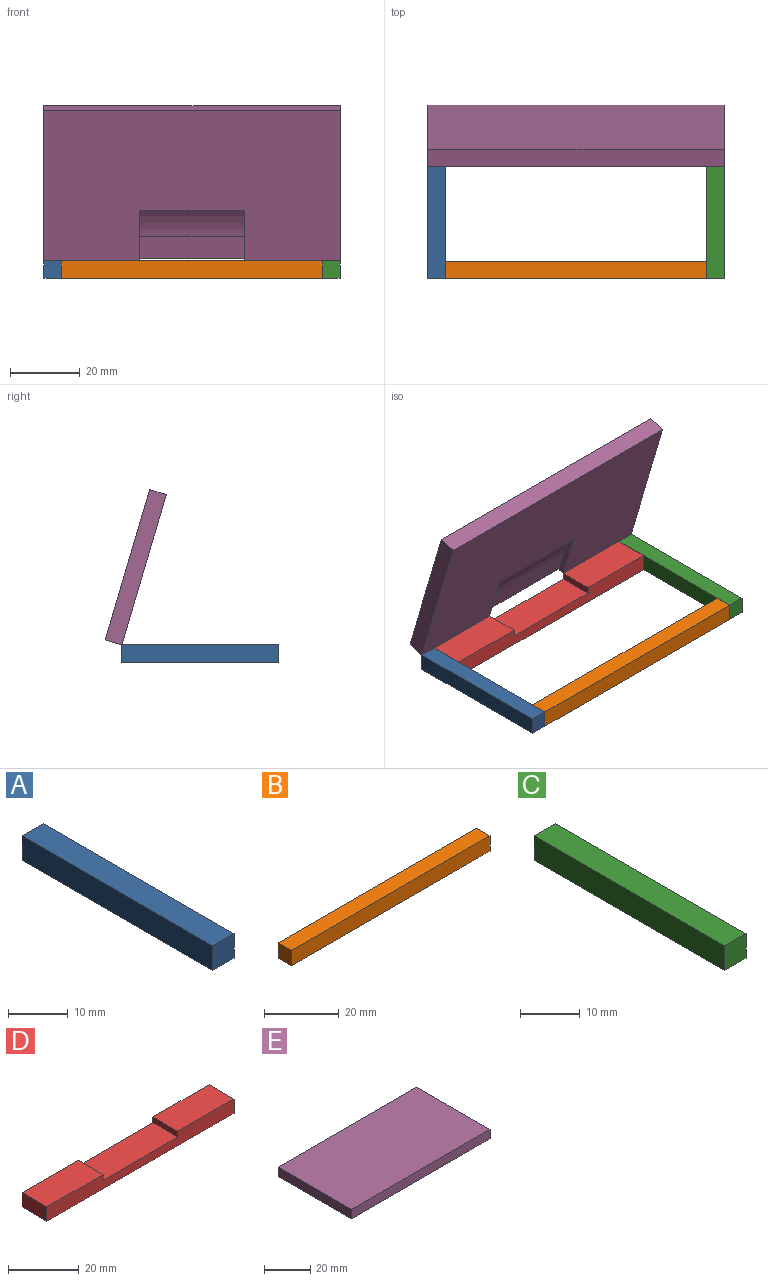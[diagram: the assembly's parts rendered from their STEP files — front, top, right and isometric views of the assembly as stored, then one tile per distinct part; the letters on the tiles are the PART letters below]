
ASSEMBLY  parts=5 mates=4
PART A: 6 faces, bbox 5x45x5 mm
  f0: plane 45x5mm, normal (1,0,0), area 225mm2, adj f1,f3,f4,f5
  f1: plane 5x5mm, normal (0,1,0), area 25mm2, adj f0,f2,f4,f5
  f2: plane 45x5mm, normal (-1,0,0), area 225mm2, adj f1,f3,f4,f5
  f3: plane 5x5mm, normal (0,-1,0), area 25mm2, adj f0,f2,f4,f5
  f4: plane 45x5mm, normal (0,0,1), area 225mm2, adj f0,f1,f2,f3
  f5: plane 45x5mm, normal (0,0,-1), area 225mm2, adj f0,f1,f2,f3
PART B: 6 faces, bbox 75x5x5 mm
  f0: plane 75x5mm, normal (0,1,0), area 375mm2, adj f1,f3,f4,f5
  f1: plane 5x5mm, normal (-1,0,0), area 25mm2, adj f0,f2,f4,f5
  f2: plane 75x5mm, normal (0,-1,0), area 375mm2, adj f1,f3,f4,f5
  f3: plane 5x5mm, normal (1,0,0), area 25mm2, adj f0,f2,f4,f5
  f4: plane 75x5mm, normal (0,0,1), area 375mm2, adj f0,f1,f2,f3
  f5: plane 75x5mm, normal (0,0,-1), area 375mm2, adj f0,f1,f2,f3
PART C: 6 faces, bbox 5x45x5 mm
  f0: plane 45x5mm, normal (-1,0,0), area 225mm2, adj f1,f3,f4,f5
  f1: plane 5x5mm, normal (0,-1,0), area 25mm2, adj f0,f2,f4,f5
  f2: plane 45x5mm, normal (1,0,0), area 225mm2, adj f1,f3,f4,f5
  f3: plane 5x5mm, normal (0,1,0), area 25mm2, adj f0,f2,f4,f5
  f4: plane 45x5mm, normal (0,0,1), area 225mm2, adj f0,f1,f2,f3
  f5: plane 45x5mm, normal (0,0,-1), area 225mm2, adj f0,f1,f2,f3
PART D: 10 faces, bbox 75x10x5 mm
  f0: plane 22.5x10mm, normal (0,0,1), area 225mm2, adj f1,f3,f4,f8
  f1: plane 75x5mm, normal (0,1,0), area 315mm2, adj f0,f2,f4,f5,f6,f7,f8,f9
  f2: plane 10x5mm, normal (-1,0,0), area 50mm2, adj f1,f3,f5,f6
  f3: plane 75x5mm, normal (0,-1,0), area 315mm2, adj f0,f2,f4,f5,f6,f7,f8,f9
  f4: plane 10x5mm, normal (1,0,0), area 50mm2, adj f0,f1,f3,f6
  f5: plane 22.5x10mm, normal (0,0,1), area 225mm2, adj f1,f2,f3,f7
  f6: plane 75x10mm, normal (0,0,-1), area 750mm2, adj f1,f2,f3,f4
  f7: plane 10x2mm, normal (1,0,0), area 20mm2, adj f1,f3,f5,f9
  f8: plane 10x2mm, normal (-1,0,0), area 20mm2, adj f0,f1,f3,f9
  f9: plane 30x10mm, normal (0,0,1), area 300mm2, adj f1,f3,f7,f8
PART E: 10 faces, bbox 85x45x5 mm
  f0: plane 85x5mm, normal (0,1,0), area 365mm2, adj f1,f2,f4,f5,f6,f7,f8
  f1: plane 85x45mm, normal (0,0,-1), area 3375mm2, adj f0,f2,f3,f4,f6,f7,f9
  f2: plane 45x5mm, normal (-1,0,0), area 225mm2, adj f0,f1,f3,f5
  f3: plane 85x5mm, normal (0,-1,0), area 425mm2, adj f1,f2,f4,f5
  f4: plane 45x5mm, normal (1,0,0), area 225mm2, adj f0,f1,f3,f5
  f5: plane 85x45mm, normal (0,0,1), area 3825mm2, adj f0,f2,f3,f4
  f6: plane 15x2mm, normal (1,0,0), area 24.6mm2, adj f0,f1,f8,f9
  f7: plane 15x2mm, normal (-1,0,0), area 24.6mm2, adj f0,f1,f8,f9
  f8: plane 30x6.75mm, normal (0,0,-1), area 202.6mm2, adj f0,f6,f7,f9
  f9: cylinder r=18mm len=30mm, axis (1,0,0), area 257mm2, adj f1,f6,f7,f8
PLACE A t=(0,-20,0)mm
PLACE B rot(axis=(0,1,0),180deg) t=(0,-20,5)mm
PLACE C t=(0,-20,0)mm
PLACE D t=(0,-20,0)mm
PLACE E rot(axis=(-1,0,0),73.5deg) t=(0,-2.08,28.98)mm
MATE fastened A.f0 <-> D.f2  axis (1,0,0) through (-37.5,5,2.5)mm
MATE fastened B.f1 <-> C.f0  axis (1,0,0) through (37.5,-40,2.5)mm
MATE revolute E.f2 <-> A.f2  axis (-1,0,0) through (-42.5,5,5)mm
MATE fastened B.f3 <-> A.f0  axis (-1,0,0) through (-37.5,-40,2.5)mm
